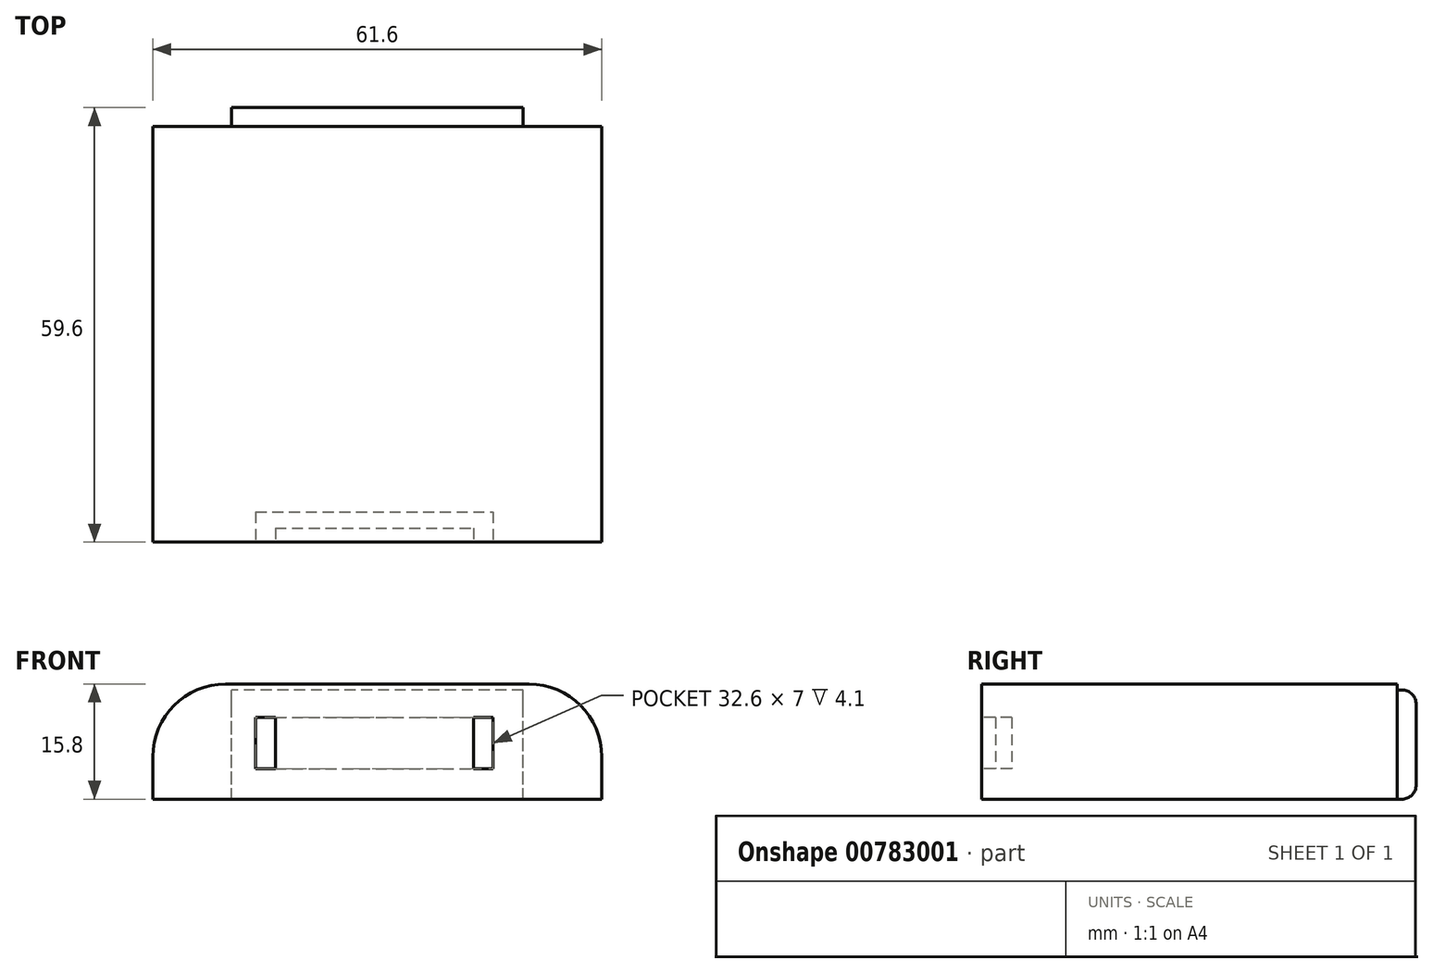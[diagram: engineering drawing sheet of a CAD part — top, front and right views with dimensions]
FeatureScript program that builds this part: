
annotation { "Feature Type Name" : "Feature", "Feature Type Description" : "" }
export const myFeature = defineFeature(function(context is Context, id is Id, definition is map)
    precondition{}
    {
        {
            var Q0;
            Q0=qCreatedBy(makeId("Front.planeOp"),FACE);
            var sketch = newSketch(context, id + "F0", { "sketchPlane" : qUnion([Q0])});
            skLineSegment(sketch, "E0.bottom", {"start": v(-20.8, 15.8) * mm, "end": v(20.8, 15.8) * mm});
            skLineSegment(sketch, "E0.top", {"start": v(-30.8, 0) * mm, "end": v(30.8, 0) * mm});
            skLineSegment(sketch, "E0.left", {"start": v(-30.8, 5.8) * mm, "end": v(-30.8, 0) * mm});
            skLineSegment(sketch, "E0.right", {"start": v(30.8, 5.8) * mm, "end": v(30.8, 0) * mm});
            skPoint(sketch, "E1.visualSharp", {"position": v(-30.8, 15.8) * mm});
            skArc(sketch, "E1.filletArc", {"start": v(-20.8, 15.8) * mm, "mid": v(-27.87, 12.87) * mm, "end": v(-30.8, 5.8) * mm});
            skPoint(sketch, "E2.visualSharp", {"position": v(30.8, 15.8) * mm});
            skArc(sketch, "E2.filletArc", {"start": v(30.8, 5.8) * mm, "mid": v(27.87, 12.87) * mm, "end": v(20.8, 15.8) * mm});
            skSolve(sketch);
        }
        {
            var Q0;
            Q0 = qSketchRegion(id + "F0", true);
            extrude(context, id + "F1", {"entities" : qUnion([Q0]), "depth" : 57 * mm, "offsetDistance" : 25 * mm});
        }
        {
            var Q0;
            Q0=qCreatedBy(makeId("Right.planeOp"),FACE);
            var sketch = newSketch(context, id + "F2", { "sketchPlane" : qUnion([Q0])});
            skLineSegment(sketch, "E3.bottom", {"start": v(0, 0) * mm, "end": v(0.6, 0) * mm});
            skLineSegment(sketch, "E3.top", {"start": v(0, 15) * mm, "end": v(0.6, 15) * mm});
            skLineSegment(sketch, "E3.left", {"start": v(0, 0) * mm, "end": v(0, 15) * mm});
            skLineSegment(sketch, "E3.right", {"start": v(2.6, 2) * mm, "end": v(2.6, 13) * mm});
            skPoint(sketch, "E4.visualSharp", {"position": v(2.6, 15) * mm});
            skArc(sketch, "E4.filletArc", {"start": v(2.6, 13) * mm, "mid": v(2.01, 14.41) * mm, "end": v(0.6, 15) * mm});
            skPoint(sketch, "E5.visualSharp", {"position": v(2.6, 0) * mm});
            skArc(sketch, "E5.filletArc", {"start": v(0.6, 0) * mm, "mid": v(2.01, 0.59) * mm, "end": v(2.6, 2) * mm});
            skSolve(sketch);
        }
        {
            var Q0;
            Q0 = qSketchRegion(id + "F2", true);
            extrude(context, id + "F3", {"entities" : qUnion([Q0]), "operationType" : NewBodyOperationType.ADD, "endBound" : BoundingType.SYMMETRIC, "depth" : 40 * mm, "offsetDistance" : 25 * mm});
        }
        {
            var Q0;
            Q0=makeQuery(id+"F1.opExtrude","CAP_FACE",FACE,{"disambiguationData":[OSD([sQuery(id+"F0.wireOp",EDGE,"E0.bottom"),sQuery(id+"F0.wireOp",EDGE,"E0.top"),sQuery(id+"F0.wireOp",EDGE,"E0.left"),sQuery(id+"F0.wireOp",EDGE,"E0.right"),sQuery(id+"F0.wireOp",EDGE,"E1.filletArc"),sQuery(id+"F0.wireOp",EDGE,"E2.filletArc")])],"isStart":false});
            var sketch = newSketch(context, id + "F4", { "sketchPlane" : qUnion([Q0])});
            skLineSegment(sketch, "E6.bottom", {"start": v(-16.7, 11.2) * mm, "end": v(-14, 11.2) * mm});
            skLineSegment(sketch, "E6.top", {"start": v(-16.7, 4.2) * mm, "end": v(-14, 4.2) * mm});
            skLineSegment(sketch, "E6.left", {"start": v(-16.7, 11.2) * mm, "end": v(-16.7, 4.2) * mm});
            skLineSegment(sketch, "E6.right", {"start": v(-14, 11.2) * mm, "end": v(-14, 4.2) * mm});
            skLineSegment(sketch, "E7.bottom", {"start": v(13.2, 11.2) * mm, "end": v(15.9, 11.2) * mm});
            skLineSegment(sketch, "E7.top", {"start": v(13.2, 4.2) * mm, "end": v(15.9, 4.2) * mm});
            skLineSegment(sketch, "E7.left", {"start": v(13.2, 11.2) * mm, "end": v(13.2, 4.2) * mm});
            skLineSegment(sketch, "E7.right", {"start": v(15.9, 11.2) * mm, "end": v(15.9, 4.2) * mm});
            skLineSegment(sketch, "E8", {"start": v(-14, 4.2) * mm, "end": v(13.2, 4.2) * mm});
            skLineSegment(sketch, "E9", {"start": v(-14, 11.2) * mm, "end": v(13.2, 11.2) * mm});
            skSolve(sketch);
        }
        {
            var Q0;
            Q0 = qSketchRegion(id + "F4", true);
            extrude(context, id + "F5", {"entities" : qUnion([Q0]), "operationType" : NewBodyOperationType.REMOVE, "oppositeDirection" : true, "depth" : 4.1 * mm, "offsetDistance" : 25 * mm});
        }
        {
            var Q0;
            Q0=makeQuery(id+"F4.imprint","IMPRINT",FACE,{"disambiguationData":[TD([[makeQuery(id+"F4.imprint","IMPRINT",EDGE,{"derivedFrom":sQuery(id+"F4.wireOp",EDGE,"E6.right")}),1.0]])]});
            extrude(context, id + "F6", {"entities" : qUnion([Q0]), "operationType" : NewBodyOperationType.ADD, "oppositeDirection" : true, "depth" : 1.9 * mm, "offsetDistance" : 25 * mm});
        }
    });
